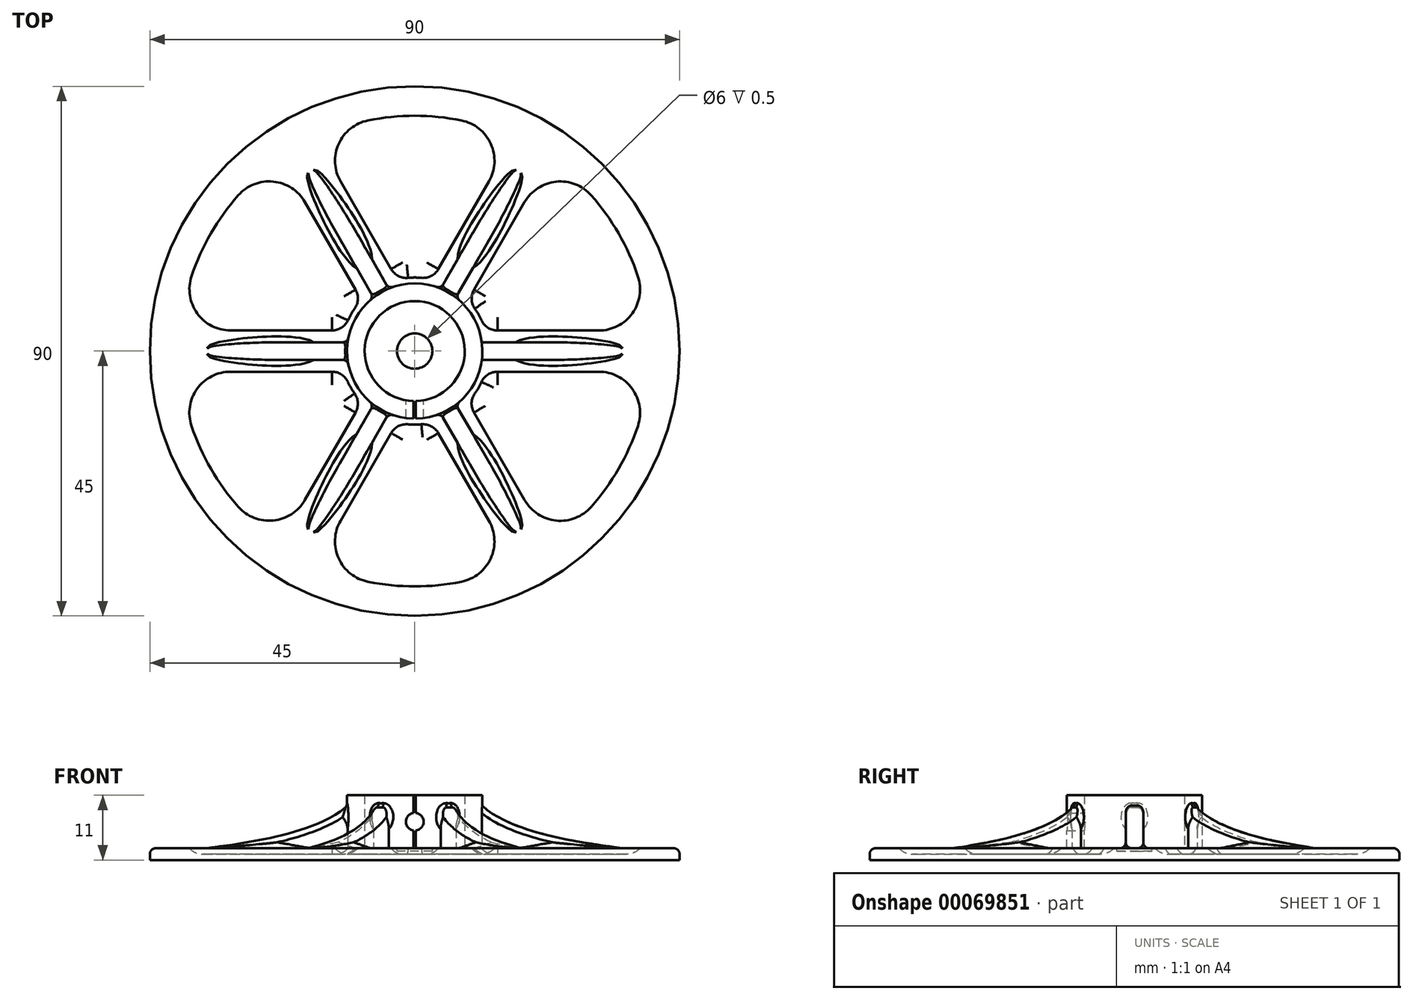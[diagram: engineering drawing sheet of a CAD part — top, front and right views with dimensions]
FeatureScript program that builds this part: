
annotation { "Feature Type Name" : "Feature", "Feature Type Description" : "" }
export const myFeature = defineFeature(function(context is Context, id is Id, definition is map)
    precondition{}
    {
        {
            var Q0;
            Q0=qCreatedBy(makeId("Top.planeOp"),FACE);
            var sketch = newSketch(context, id + "F0", { "sketchPlane" : qUnion([Q0])});
            skCircle(sketch, "E0", {"center": v(0, 0) * mm, "radius": 45 * mm});
            skSolve(sketch);
        }
        {
            var Q0;
            Q0 = qSketchRegion(id + "F0", true);
            extrude(context, id + "F1", {"entities" : qUnion([Q0]), "depth" : 2 * mm});
        }
        {
            var Q0;
            Q0=makeQuery(id+"F1.opExtrude","CAP_FACE",FACE,{"disambiguationData":[OSD([sQuery(id+"F0.wireOp",EDGE,"E0")])],"isStart":false});
            var sketch = newSketch(context, id + "F2", { "sketchPlane" : qUnion([Q0])});
            skCircle(sketch, "E1", {"center": v(0, 0) * mm, "radius": 8.5 * mm});
            skCircle(sketch, "E2", {"center": v(0, 0) * mm, "radius": 11.5 * mm});
            skSolve(sketch);
        }
        {
            var Q0;
            Q0 = qSketchRegion(id + "F2", true);
            extrude(context, id + "F3", {"entities" : qUnion([Q0]), "operationType" : NewBodyOperationType.ADD, "depth" : 9 * mm});
        }
        {
            var Q0;
            Q0=qCreatedBy(makeId("Front.planeOp"),FACE);
            var sketch = newSketch(context, id + "F4", { "sketchPlane" : qUnion([Q0])});
            skLineSegment(sketch, "E3.0", {"start": v(-11.5, 11) * mm, "end": v(11.5, 11) * mm});
            skLineSegment(sketch, "E3.1", {"start": v(-11.5, 2) * mm, "end": v(11.5, 2) * mm});
            skLineSegment(sketch, "E4", {"start": v(0, 11) * mm, "end": v(0, 2) * mm, "construction": true});
            skCircle(sketch, "E5", {"center": v(0, 6.5) * mm, "radius": 1.5 * mm});
            skSolve(sketch);
        }
        {
            var Q0;
            Q0 = qSketchRegion(id + "F4", true);
            var Q1;
            Q1=makeQuery(id+"F3.opExtrude","SWEPT_FACE",FACE,{"disambiguationData":[OSD([sQuery(id+"F2.wireOp",EDGE,"E2")])]});
            extrude(context, id + "F5", {"entities" : qUnion([Q0]), "operationType" : NewBodyOperationType.REMOVE, "endBound" : BoundingType.UP_TO_SURFACE, "endBoundEntityFace" : qUnion([Q1]), "depth" : 25 * mm});
        }
        {
            var Q0;
            Q0=makeQuery(id+"F3.opExtrude","CAP_FACE",FACE,{"disambiguationData":[OSD([sQuery(id+"F2.wireOp",EDGE,"E1"),sQuery(id+"F2.wireOp",EDGE,"E2")])],"isStart":false});
            var sketch = newSketch(context, id + "F6", { "sketchPlane" : qUnion([Q0])});
            skLineSegment(sketch, "E6.rect.bottom", {"start": v(0.2, -8.5) * mm, "end": v(-0.2, -8.5) * mm});
            skLineSegment(sketch, "E6.rect.top", {"start": v(0.2, -11.5) * mm, "end": v(-0.2, -11.5) * mm});
            skLineSegment(sketch, "E6.rect.left", {"start": v(0.2, -8.5) * mm, "end": v(0.2, -11.5) * mm});
            skLineSegment(sketch, "E6.rect.right", {"start": v(-0.2, -8.5) * mm, "end": v(-0.2, -11.5) * mm});
            skPoint(sketch, "E6.rect.middle", {"position": v(0, -10) * mm});
            skSolve(sketch);
        }
        {
            var Q0;
            Q0 = qSketchRegion(id + "F6", true);
            var Q1;
            {var subQ0=sQuery(id+"F0.wireOp",EDGE,"E0");Q1=makeQuery(id+"F3.boolean.opBoolean","SPLIT",FACE,{"disambiguationData":[TD([makeQuery(id+"F1.opExtrude","SWEPT_FACE",FACE,{"disambiguationData":[OSD([subQ0])]})])],"derivedFrom":makeQuery(id+"F1.opExtrude","CAP_FACE",FACE,{"disambiguationData":[OSD([subQ0])],"isStart":false})});}
            extrude(context, id + "F7", {"entities" : qUnion([Q0]), "operationType" : NewBodyOperationType.REMOVE, "endBound" : BoundingType.UP_TO_SURFACE, "oppositeDirection" : true, "endBoundEntityFace" : qUnion([Q1]), "depth" : 25 * mm});
        }
        {
            var Q0;
            Q0=qCreatedBy(makeId("Front.planeOp"),FACE);
            var sketch = newSketch(context, id + "F8", { "sketchPlane" : qUnion([Q0])});
            skLineSegment(sketch, "E7", {"start": v(11.16, 9.67) * mm, "end": v(11.16, 1.18) * mm});
            skLineSegment(sketch, "E8", {"start": v(11.16, 1.18) * mm, "end": v(39.62, 1.18) * mm});
            skLineSegment(sketch, "E9", {"start": v(39.62, 1.18) * mm, "end": v(39.63, 1.46) * mm});
            skFitSpline(sketch, "E10", {"points": [v(11.16, 9.67) * mm, v(20.72, 4.72) * mm, v(39.63, 1.46) * mm], "startDerivative": vector(9.57, -13.36) * mm, "endDerivative": vector(30.16, -3.66) * mm});
            skSolve(sketch);
        }
        {
            var Q0;
            Q0 = qSketchRegion(id + "F8", true);
            extrude(context, id + "F9", {"entities" : qUnion([Q0]), "endBound" : BoundingType.SYMMETRIC, "depth" : 3 * mm});
        }
        {
            var Q0;
            Q0=makeQuery(id+"F9.opExtrude","SWEPT_BODY",BODY,{"disambiguationData":[OSD([sQuery(id+"F8.wireOp",EDGE,"E7"),sQuery(id+"F8.wireOp",EDGE,"E8"),sQuery(id+"F8.wireOp",EDGE,"E9"),sQuery(id+"F8.wireOp",EDGE,"E10")])]});
            var Q1;
            Q1=makeQuery(id+"F3.opExtrude","SWEPT_FACE",FACE,{"disambiguationData":[OSD([sQuery(id+"F2.wireOp",EDGE,"E1")])]});
            circularPattern(context, id + "F10", {"operationType" : NewBodyOperationType.ADD, "entities" : qUnion([Q0]), "axis" : qUnion([Q1]), "angle" : 360 * degree, "instanceCount" : 6, "equalSpace" : true});
        }
        {
            var Q0;
            Q0=makeQuery(id+"F9.opExtrude","CAP_EDGE",EDGE,{"disambiguationData":[OSD([sQuery(id+"F8.wireOp",EDGE,"E10")])],"isStart":false});
            var Q1;
            Q1=makeQuery(id+"F9.opExtrude","CAP_EDGE",EDGE,{"disambiguationData":[OSD([sQuery(id+"F8.wireOp",EDGE,"E10")])],"isStart":true});
            var Q2;
            {var subQ0=sQuery(id+"F0.wireOp",EDGE,"E0");var subQ1=makeQuery(id+"F1.opExtrude","CAP_FACE",FACE,{"disambiguationData":[OSD([subQ0])],"isStart":false});Q2=makeQuery(id+"F10.boolean.opBoolean","INTERSECT",EDGE,{"derivedFrom":[makeQuery(id+"F7.boolean.opBoolean","MERGE",FACE,{"derivedFrom":[makeQuery(id+"F3.boolean.opBoolean","SPLIT",FACE,{"disambiguationData":[TD([makeQuery(id+"F1.opExtrude","SWEPT_FACE",FACE,{"disambiguationData":[OSD([subQ0])]})])],"derivedFrom":subQ1}),makeQuery(id+"F3.boolean.opBoolean","SPLIT",FACE,{"disambiguationData":[TD([makeQuery(id+"F3.opExtrude","SWEPT_FACE",FACE,{"disambiguationData":[OSD([sQuery(id+"F2.wireOp",EDGE,"E1")])]})])],"derivedFrom":subQ1}),makeQuery(id+"F7.opExtrude","CAP_FACE",FACE,{"disambiguationData":[OSD([sQuery(id+"F6.wireOp",EDGE,"E6.rect.bottom"),sQuery(id+"F6.wireOp",EDGE,"E6.rect.top"),sQuery(id+"F6.wireOp",EDGE,"E6.rect.left"),sQuery(id+"F6.wireOp",EDGE,"E6.rect.right")])],"isStart":false})]}),makeQuery(id+"F9.opExtrude","SWEPT_FACE",FACE,{"disambiguationData":[OSD([sQuery(id+"F8.wireOp",EDGE,"E10")])]})]});}
            var Q3;
            {var subQ0=sQuery(id+"F0.wireOp",EDGE,"E0");var subQ1=makeQuery(id+"F1.opExtrude","CAP_FACE",FACE,{"disambiguationData":[OSD([subQ0])],"isStart":false});Q3=makeQuery(id+"F10.boolean.opBoolean","INTERSECT",EDGE,{"derivedFrom":[makeQuery(id+"F7.boolean.opBoolean","MERGE",FACE,{"derivedFrom":[makeQuery(id+"F3.boolean.opBoolean","SPLIT",FACE,{"disambiguationData":[TD([makeQuery(id+"F1.opExtrude","SWEPT_FACE",FACE,{"disambiguationData":[OSD([subQ0])]})])],"derivedFrom":subQ1}),makeQuery(id+"F3.boolean.opBoolean","SPLIT",FACE,{"disambiguationData":[TD([makeQuery(id+"F3.opExtrude","SWEPT_FACE",FACE,{"disambiguationData":[OSD([sQuery(id+"F2.wireOp",EDGE,"E1")])]})])],"derivedFrom":subQ1}),makeQuery(id+"F7.opExtrude","CAP_FACE",FACE,{"disambiguationData":[OSD([sQuery(id+"F6.wireOp",EDGE,"E6.rect.bottom"),sQuery(id+"F6.wireOp",EDGE,"E6.rect.top"),sQuery(id+"F6.wireOp",EDGE,"E6.rect.left"),sQuery(id+"F6.wireOp",EDGE,"E6.rect.right")])],"isStart":false})]}),makeQuery(id+"F10.opPattern","COPY",FACE,{"derivedFrom":makeQuery(id+"F9.opExtrude","SWEPT_FACE",FACE,{"disambiguationData":[OSD([sQuery(id+"F8.wireOp",EDGE,"E10")])]}),"instanceName":"5"})]});}
            var Q4;
            Q4=makeQuery(id+"F10.opPattern","COPY",FACE,{"derivedFrom":makeQuery(id+"F9.opExtrude","SWEPT_FACE",FACE,{"disambiguationData":[OSD([sQuery(id+"F8.wireOp",EDGE,"E10")])]}),"instanceName":"5"});
            var Q5;
            Q5=makeQuery(id+"F10.opPattern","COPY",FACE,{"derivedFrom":makeQuery(id+"F9.opExtrude","SWEPT_FACE",FACE,{"disambiguationData":[OSD([sQuery(id+"F8.wireOp",EDGE,"E10")])]}),"instanceName":"4"});
            var Q6;
            Q6=makeQuery(id+"F10.opPattern","COPY",FACE,{"derivedFrom":makeQuery(id+"F9.opExtrude","SWEPT_FACE",FACE,{"disambiguationData":[OSD([sQuery(id+"F8.wireOp",EDGE,"E10")])]}),"instanceName":"3"});
            var Q7;
            Q7=makeQuery(id+"F10.opPattern","COPY",FACE,{"derivedFrom":makeQuery(id+"F9.opExtrude","SWEPT_FACE",FACE,{"disambiguationData":[OSD([sQuery(id+"F8.wireOp",EDGE,"E10")])]}),"instanceName":"1"});
            var Q8;
            Q8=makeQuery(id+"F10.opPattern","COPY",FACE,{"derivedFrom":makeQuery(id+"F9.opExtrude","SWEPT_FACE",FACE,{"disambiguationData":[OSD([sQuery(id+"F8.wireOp",EDGE,"E10")])]}),"instanceName":"2"});
            fillet(context, id + "F11", {"entities" : qUnion([Q0, Q1, Q2, Q3, Q4, Q5, Q6, Q7, Q8]), "radius" : 1 * mm, "tangentPropagation" : true, "allowEdgeOverflow" : false});
        }
        {
            var Q0;
            {var subQ0=sQuery(id+"F0.wireOp",EDGE,"E0");var subQ1=makeQuery(id+"F1.opExtrude","CAP_FACE",FACE,{"disambiguationData":[OSD([subQ0])],"isStart":false});Q0=makeQuery(id+"F7.boolean.opBoolean","MERGE",FACE,{"derivedFrom":[makeQuery(id+"F3.boolean.opBoolean","SPLIT",FACE,{"disambiguationData":[TD([makeQuery(id+"F1.opExtrude","SWEPT_FACE",FACE,{"disambiguationData":[OSD([subQ0])]})])],"derivedFrom":subQ1}),makeQuery(id+"F3.boolean.opBoolean","SPLIT",FACE,{"disambiguationData":[TD([makeQuery(id+"F3.opExtrude","SWEPT_FACE",FACE,{"disambiguationData":[OSD([sQuery(id+"F2.wireOp",EDGE,"E1")])]})])],"derivedFrom":subQ1}),makeQuery(id+"F7.opExtrude","CAP_FACE",FACE,{"disambiguationData":[OSD([sQuery(id+"F6.wireOp",EDGE,"E6.rect.bottom"),sQuery(id+"F6.wireOp",EDGE,"E6.rect.top"),sQuery(id+"F6.wireOp",EDGE,"E6.rect.left"),sQuery(id+"F6.wireOp",EDGE,"E6.rect.right")])],"isStart":false})]});}
            var sketch = newSketch(context, id + "F12", { "sketchPlane" : qUnion([Q0])});
            skPoint(sketch, "E11.1.end.orphan", {"position": v(-0.2, -11.5) * mm});
            skPoint(sketch, "E11.1.start.orphan", {"position": v(0.2, -11.5) * mm});
            skLineSegment(sketch, "E12.0", {"start": v(14.07, 3.5) * mm, "end": v(31.28, 3.5) * mm});
            skArc(sketch, "E12.1", {"start": v(11.35, 5.24) * mm, "mid": v(10.83, 6.25) * mm, "end": v(10.21, 7.2) * mm});
            skLineSegment(sketch, "E12.2", {"start": v(18.67, 25.34) * mm, "end": v(10.07, 10.44) * mm});
            skArc(sketch, "E13", {"start": v(37.92, 12.73) * mm, "mid": v(34.64, 20) * mm, "end": v(29.98, 26.48) * mm});
            skPoint(sketch, "E14.visualSharp", {"position": v(22.95, 32.76) * mm});
            skArc(sketch, "E14.filletArc", {"start": v(29.98, 26.48) * mm, "mid": v(24.04, 28.8) * mm, "end": v(18.67, 25.34) * mm});
            skPoint(sketch, "E15.visualSharp", {"position": v(39.85, 3.5) * mm});
            skArc(sketch, "E15.filletArc", {"start": v(31.28, 3.5) * mm, "mid": v(36.97, 6.41) * mm, "end": v(37.92, 12.73) * mm});
            skPoint(sketch, "E16.visualSharp", {"position": v(12, 3.5) * mm});
            skArc(sketch, "E16.filletArc", {"start": v(11.35, 5.24) * mm, "mid": v(12.45, 3.97) * mm, "end": v(14.07, 3.5) * mm});
            skPoint(sketch, "E17.visualSharp", {"position": v(9.03, 8.64) * mm});
            skArc(sketch, "E17.filletArc", {"start": v(10.07, 10.44) * mm, "mid": v(9.67, 8.8) * mm, "end": v(10.21, 7.2) * mm});
            skSolve(sketch);
        }
        {
            var Q0;
            Q0 = qSketchRegion(id + "F12", true);
            extrude(context, id + "F13", {"entities" : qUnion([Q0]), "oppositeDirection" : true, "depth" : 1 * mm});
        }
        {
            var Q0;
            Q0=makeQuery(id+"F13.opExtrude","SWEPT_BODY",BODY,{"disambiguationData":[OSD([sQuery(id+"F12.wireOp",EDGE,"E12.0"),sQuery(id+"F12.wireOp",EDGE,"E12.1"),sQuery(id+"F12.wireOp",EDGE,"E12.2"),sQuery(id+"F12.wireOp",EDGE,"E13"),sQuery(id+"F12.wireOp",EDGE,"E14.filletArc"),sQuery(id+"F12.wireOp",EDGE,"E15.filletArc"),sQuery(id+"F12.wireOp",EDGE,"E16.filletArc"),sQuery(id+"F12.wireOp",EDGE,"E17.filletArc")])]});
            var Q1;
            Q1=makeQuery(id+"F3.opExtrude","SWEPT_FACE",FACE,{"disambiguationData":[OSD([sQuery(id+"F2.wireOp",EDGE,"E1")])]});
            circularPattern(context, id + "F14", {"operationType" : NewBodyOperationType.REMOVE, "entities" : qUnion([Q0]), "axis" : qUnion([Q1]), "angle" : 360 * degree, "instanceCount" : 6, "equalSpace" : true});
        }
        {
            var Q0;
            Q0=makeQuery(id+"F14.boolean.opBoolean","COPY",FACE,{"derivedFrom":makeQuery(id+"F13.opExtrude","CAP_FACE",FACE,{"disambiguationData":[OSD([sQuery(id+"F12.wireOp",EDGE,"E12.0"),sQuery(id+"F12.wireOp",EDGE,"E12.1"),sQuery(id+"F12.wireOp",EDGE,"E12.2"),sQuery(id+"F12.wireOp",EDGE,"E13"),sQuery(id+"F12.wireOp",EDGE,"E14.filletArc"),sQuery(id+"F12.wireOp",EDGE,"E15.filletArc"),sQuery(id+"F12.wireOp",EDGE,"E16.filletArc"),sQuery(id+"F12.wireOp",EDGE,"E17.filletArc")])],"isStart":false})});
            var Q1;
            Q1=makeQuery(id+"F14.boolean.opBoolean","COPY",FACE,{"derivedFrom":makeQuery(id+"F14.opPattern","COPY",FACE,{"derivedFrom":makeQuery(id+"F13.opExtrude","CAP_FACE",FACE,{"disambiguationData":[OSD([sQuery(id+"F12.wireOp",EDGE,"E12.0"),sQuery(id+"F12.wireOp",EDGE,"E12.1"),sQuery(id+"F12.wireOp",EDGE,"E12.2"),sQuery(id+"F12.wireOp",EDGE,"E13"),sQuery(id+"F12.wireOp",EDGE,"E14.filletArc"),sQuery(id+"F12.wireOp",EDGE,"E15.filletArc"),sQuery(id+"F12.wireOp",EDGE,"E16.filletArc"),sQuery(id+"F12.wireOp",EDGE,"E17.filletArc")])],"isStart":false}),"instanceName":"1"})});
            var Q2;
            Q2=makeQuery(id+"F14.boolean.opBoolean","COPY",FACE,{"derivedFrom":makeQuery(id+"F14.opPattern","COPY",FACE,{"derivedFrom":makeQuery(id+"F13.opExtrude","CAP_FACE",FACE,{"disambiguationData":[OSD([sQuery(id+"F12.wireOp",EDGE,"E12.0"),sQuery(id+"F12.wireOp",EDGE,"E12.1"),sQuery(id+"F12.wireOp",EDGE,"E12.2"),sQuery(id+"F12.wireOp",EDGE,"E13"),sQuery(id+"F12.wireOp",EDGE,"E14.filletArc"),sQuery(id+"F12.wireOp",EDGE,"E15.filletArc"),sQuery(id+"F12.wireOp",EDGE,"E16.filletArc"),sQuery(id+"F12.wireOp",EDGE,"E17.filletArc")])],"isStart":false}),"instanceName":"2"})});
            var Q3;
            Q3=makeQuery(id+"F14.boolean.opBoolean","COPY",FACE,{"derivedFrom":makeQuery(id+"F14.opPattern","COPY",FACE,{"derivedFrom":makeQuery(id+"F13.opExtrude","CAP_FACE",FACE,{"disambiguationData":[OSD([sQuery(id+"F12.wireOp",EDGE,"E12.0"),sQuery(id+"F12.wireOp",EDGE,"E12.1"),sQuery(id+"F12.wireOp",EDGE,"E12.2"),sQuery(id+"F12.wireOp",EDGE,"E13"),sQuery(id+"F12.wireOp",EDGE,"E14.filletArc"),sQuery(id+"F12.wireOp",EDGE,"E15.filletArc"),sQuery(id+"F12.wireOp",EDGE,"E16.filletArc"),sQuery(id+"F12.wireOp",EDGE,"E17.filletArc")])],"isStart":false}),"instanceName":"3"})});
            var Q4;
            Q4=makeQuery(id+"F14.boolean.opBoolean","COPY",FACE,{"derivedFrom":makeQuery(id+"F14.opPattern","COPY",FACE,{"derivedFrom":makeQuery(id+"F13.opExtrude","CAP_FACE",FACE,{"disambiguationData":[OSD([sQuery(id+"F12.wireOp",EDGE,"E12.0"),sQuery(id+"F12.wireOp",EDGE,"E12.1"),sQuery(id+"F12.wireOp",EDGE,"E12.2"),sQuery(id+"F12.wireOp",EDGE,"E13"),sQuery(id+"F12.wireOp",EDGE,"E14.filletArc"),sQuery(id+"F12.wireOp",EDGE,"E15.filletArc"),sQuery(id+"F12.wireOp",EDGE,"E16.filletArc"),sQuery(id+"F12.wireOp",EDGE,"E17.filletArc")])],"isStart":false}),"instanceName":"4"})});
            var Q5;
            Q5=makeQuery(id+"F14.boolean.opBoolean","COPY",FACE,{"derivedFrom":makeQuery(id+"F14.opPattern","COPY",FACE,{"derivedFrom":makeQuery(id+"F13.opExtrude","CAP_FACE",FACE,{"disambiguationData":[OSD([sQuery(id+"F12.wireOp",EDGE,"E12.0"),sQuery(id+"F12.wireOp",EDGE,"E12.1"),sQuery(id+"F12.wireOp",EDGE,"E12.2"),sQuery(id+"F12.wireOp",EDGE,"E13"),sQuery(id+"F12.wireOp",EDGE,"E14.filletArc"),sQuery(id+"F12.wireOp",EDGE,"E15.filletArc"),sQuery(id+"F12.wireOp",EDGE,"E16.filletArc"),sQuery(id+"F12.wireOp",EDGE,"E17.filletArc")])],"isStart":false}),"instanceName":"5"})});
            fillet(context, id + "F15", {"entities" : qUnion([Q0, Q1, Q2, Q3, Q4, Q5]), "radius" : 3 * mm, "tangentPropagation" : true, "allowEdgeOverflow" : false});
        }
        {
            var Q0;
            Q0=makeQuery(id+"F1.opExtrude","CAP_EDGE",EDGE,{"disambiguationData":[OSD([sQuery(id+"F0.wireOp",EDGE,"E0")])],"isStart":false});
            fillet(context, id + "F16", {"entities" : qUnion([Q0]), "radius" : 1 * mm, "tangentPropagation" : true, "allowEdgeOverflow" : false});
        }
        {
            var Q0;
            {var subQ0=sQuery(id+"F0.wireOp",EDGE,"E0");var subQ1=makeQuery(id+"F1.opExtrude","CAP_FACE",FACE,{"disambiguationData":[OSD([subQ0])],"isStart":false});Q0=makeQuery(id+"F7.boolean.opBoolean","MERGE",FACE,{"derivedFrom":[makeQuery(id+"F3.boolean.opBoolean","SPLIT",FACE,{"disambiguationData":[TD([makeQuery(id+"F1.opExtrude","SWEPT_FACE",FACE,{"disambiguationData":[OSD([subQ0])]})])],"derivedFrom":subQ1}),makeQuery(id+"F3.boolean.opBoolean","SPLIT",FACE,{"disambiguationData":[TD([makeQuery(id+"F3.opExtrude","SWEPT_FACE",FACE,{"disambiguationData":[OSD([sQuery(id+"F2.wireOp",EDGE,"E1")])]})])],"derivedFrom":subQ1}),makeQuery(id+"F7.opExtrude","CAP_FACE",FACE,{"disambiguationData":[OSD([sQuery(id+"F6.wireOp",EDGE,"E6.rect.bottom"),sQuery(id+"F6.wireOp",EDGE,"E6.rect.top"),sQuery(id+"F6.wireOp",EDGE,"E6.rect.left"),sQuery(id+"F6.wireOp",EDGE,"E6.rect.right")])],"isStart":false})]});}
            var sketch = newSketch(context, id + "F17", { "sketchPlane" : qUnion([Q0])});
            skCircle(sketch, "E18", {"center": v(0, 0) * mm, "radius": 3 * mm});
            skSolve(sketch);
        }
        {
            var Q0;
            Q0 = qSketchRegion(id + "F17", true);
            extrude(context, id + "F18", {"entities" : qUnion([Q0]), "operationType" : NewBodyOperationType.REMOVE, "oppositeDirection" : true, "depth" : 0.5 * mm});
        }
    });
